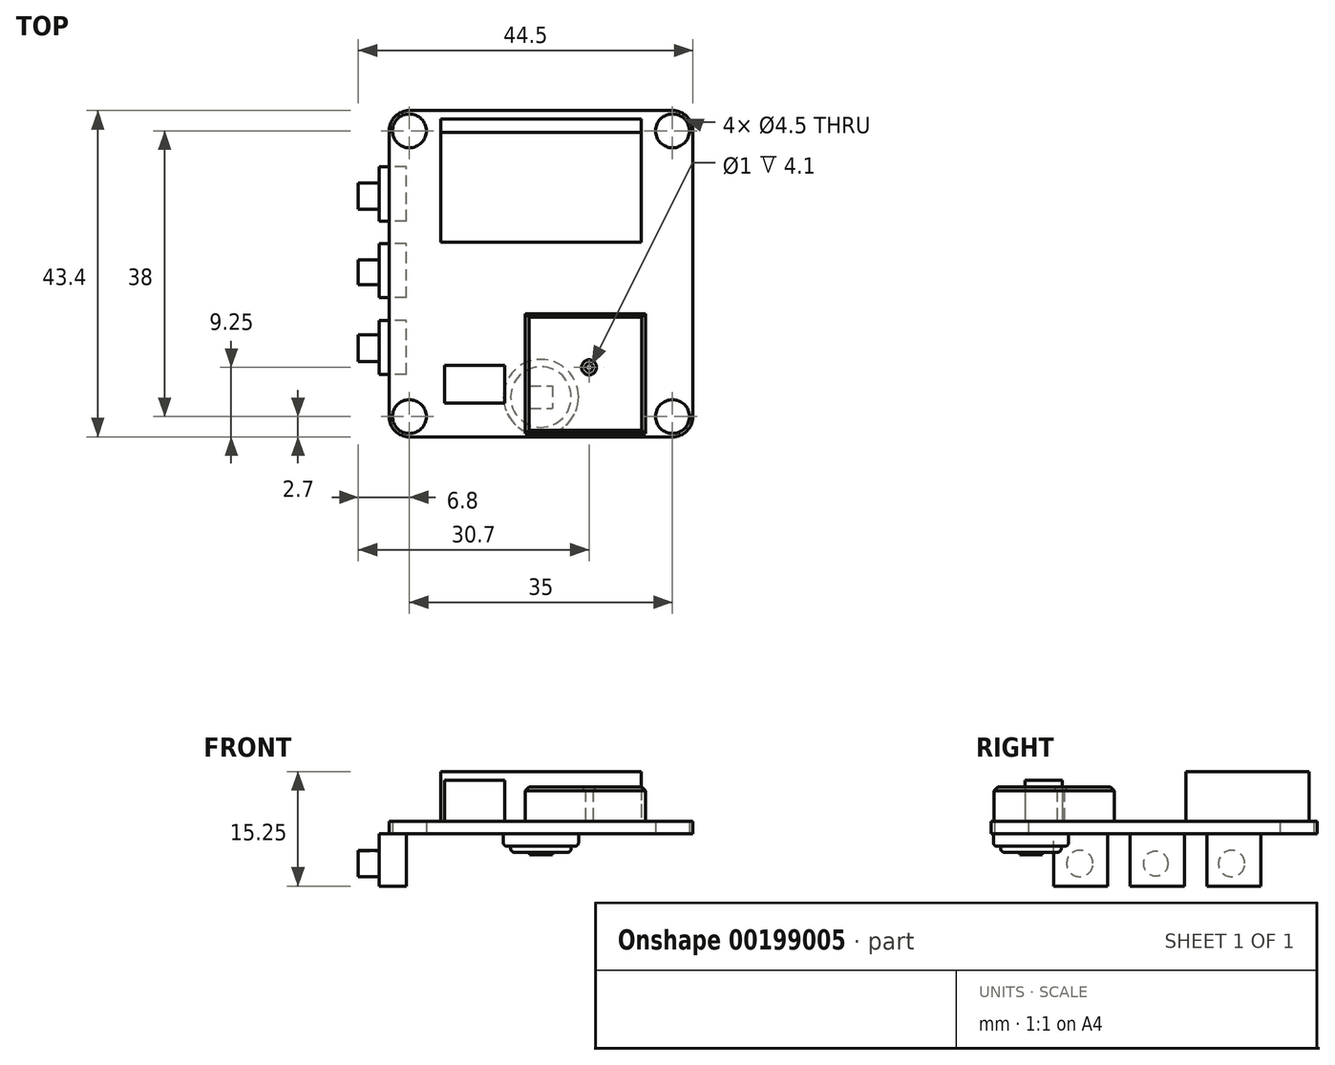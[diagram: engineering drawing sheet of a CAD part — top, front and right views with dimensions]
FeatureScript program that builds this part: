
annotation { "Feature Type Name" : "Feature", "Feature Type Description" : "" }
export const myFeature = defineFeature(function(context is Context, id is Id, definition is map)
    precondition{}
    {
        {
            var Q0;
            Q0=qCreatedBy(makeId("Top.planeOp"),FACE);
            var sketch = newSketch(context, id + "F0", { "sketchPlane" : qUnion([Q0])});
            skLineSegment(sketch, "E0.bottom", {"start": v(17.5, -21.7) * mm, "end": v(-17.5, -21.7) * mm});
            skLineSegment(sketch, "E0.top", {"start": v(17.5, 21.7) * mm, "end": v(-17.5, 21.7) * mm});
            skLineSegment(sketch, "E0.left", {"start": v(20.2, -19) * mm, "end": v(20.2, 19) * mm});
            skLineSegment(sketch, "E0.right", {"start": v(-20.2, -19) * mm, "end": v(-20.2, 19) * mm});
            skPoint(sketch, "E0.middle", {"position": v(0, 0) * mm});
            skPoint(sketch, "E1.visualSharp", {"position": v(-20.2, 21.7) * mm});
            skArc(sketch, "E1.filletArc", {"start": v(-17.5, 21.7) * mm, "mid": v(-19.4, 20.9) * mm, "end": v(-20.2, 19) * mm});
            skPoint(sketch, "E2.visualSharp", {"position": v(-20.2, -21.7) * mm});
            skArc(sketch, "E2.filletArc", {"start": v(-20.2, -19) * mm, "mid": v(-19.4, -20.9) * mm, "end": v(-17.5, -21.7) * mm});
            skPoint(sketch, "E3.visualSharp", {"position": v(20.2, -21.7) * mm});
            skArc(sketch, "E3.filletArc", {"start": v(17.5, -21.7) * mm, "mid": v(19.4, -20.9) * mm, "end": v(20.2, -19) * mm});
            skPoint(sketch, "E4.visualSharp", {"position": v(20.2, 21.7) * mm});
            skArc(sketch, "E4.filletArc", {"start": v(20.2, 19) * mm, "mid": v(19.4, 20.9) * mm, "end": v(17.5, 21.7) * mm});
            skCircle(sketch, "E5", {"center": v(-17.5, 19) * mm, "radius": 2.25 * mm});
            skCircle(sketch, "E6", {"center": v(17.5, 19) * mm, "radius": 2.25 * mm});
            skCircle(sketch, "E7", {"center": v(-17.5, -19) * mm, "radius": 2.25 * mm});
            skCircle(sketch, "E8", {"center": v(-17.5, -19) * mm, "radius": 1.5 * mm});
            skCircle(sketch, "E9", {"center": v(-17.5, 19) * mm, "radius": 1.5 * mm});
            skCircle(sketch, "E10", {"center": v(17.5, -19) * mm, "radius": 2.25 * mm});
            skCircle(sketch, "E11", {"center": v(17.5, -19) * mm, "radius": 1.5 * mm});
            skCircle(sketch, "E12", {"center": v(17.5, 19) * mm, "radius": 1.5 * mm});
            skSolve(sketch);
        }
        {
            var Q0;
            Q0 = qSketchRegion(id + "F0", true);
            extrude(context, id + "F1", {"entities" : qUnion([Q0]), "depth" : 1.6 * mm, "symmetric" : true});
        }
        {
            var Q0;
            Q0=makeQuery(id+"F1.opExtrude","CAP_FACE",FACE,{"disambiguationData":[OSD([sQuery(id+"F0.wireOp",EDGE,"E0.bottom"),sQuery(id+"F0.wireOp",EDGE,"E0.top"),sQuery(id+"F0.wireOp",EDGE,"E0.left"),sQuery(id+"F0.wireOp",EDGE,"E0.right"),sQuery(id+"F0.wireOp",EDGE,"E1.filletArc"),sQuery(id+"F0.wireOp",EDGE,"E2.filletArc"),sQuery(id+"F0.wireOp",EDGE,"E3.filletArc"),sQuery(id+"F0.wireOp",EDGE,"E4.filletArc"),sQuery(id+"F0.wireOp",EDGE,"E5"),sQuery(id+"F0.wireOp",EDGE,"E6"),sQuery(id+"F0.wireOp",EDGE,"E7"),sQuery(id+"F0.wireOp",EDGE,"E10")])],"isStart":false});
            cPlane(context, id + "F2", {"entities" : qUnion([Q0]), "cplaneType" : CPlaneType.OFFSET, "offset" : 0 * mm, "width" : 150 * mm, "height" : 150 * mm});
        }
        {
            var Q0;
            Q0=qCreatedBy(id+"F2.planeOp",FACE);
            var sketch = newSketch(context, id + "F3", { "sketchPlane" : qUnion([Q0])});
            skPoint(sketch, "E13.middle", {"position": v(0, 0) * mm});
            skPoint(sketch, "E14", {"position": v(-8.8, -14.7) * mm});
            skLineSegment(sketch, "E15.bottom", {"start": v(-4.8, -17.2) * mm, "end": v(-12.8, -17.2) * mm});
            skLineSegment(sketch, "E15.top", {"start": v(-4.8, -12.2) * mm, "end": v(-12.8, -12.2) * mm});
            skLineSegment(sketch, "E15.left", {"start": v(-4.8, -17.2) * mm, "end": v(-4.8, -12.2) * mm});
            skLineSegment(sketch, "E15.right", {"start": v(-12.8, -17.2) * mm, "end": v(-12.8, -12.2) * mm});
            skPoint(sketch, "E16", {"position": v(5.9, -13.3) * mm});
            skCircle(sketch, "E17", {"center": v(6.4, -12.45) * mm, "radius": 0.5 * mm});
            skLineSegment(sketch, "E18.bottom", {"start": v(-2.1, -5.3) * mm, "end": v(13.9, -5.3) * mm});
            skLineSegment(sketch, "E18.top", {"start": v(-2.1, -21.3) * mm, "end": v(13.9, -21.3) * mm});
            skLineSegment(sketch, "E18.left", {"start": v(-2.1, -5.3) * mm, "end": v(-2.1, -21.3) * mm});
            skLineSegment(sketch, "E18.right", {"start": v(13.9, -5.3) * mm, "end": v(13.9, -21.3) * mm});
            skLineSegment(sketch, "E19", {"start": v(-20.2, -21.7) * mm, "end": v(-13.35, -21.7) * mm});
            skLineSegment(sketch, "E20", {"start": v(-13.35, -21.7) * mm, "end": v(-13.35, -4.8) * mm});
            skLineSegment(sketch, "E21.bottom", {"start": v(-13.35, -4.8) * mm, "end": v(13.35, -4.8) * mm});
            skLineSegment(sketch, "E21.top", {"start": v(-13.35, 20.6) * mm, "end": v(13.35, 20.6) * mm});
            skLineSegment(sketch, "E21.left", {"start": v(-13.35, -4.8) * mm, "end": v(-13.35, 20.6) * mm});
            skLineSegment(sketch, "E21.right", {"start": v(13.35, -4.8) * mm, "end": v(13.35, 20.6) * mm});
            skLineSegment(sketch, "E22", {"start": v(-13.35, -4.8) * mm, "end": v(-13.35, 4.2) * mm});
            skLineSegment(sketch, "E23.bottom", {"start": v(-13.35, 4.2) * mm, "end": v(13.35, 4.2) * mm});
            skLineSegment(sketch, "E23.top", {"start": v(-13.35, 18.8) * mm, "end": v(13.35, 18.8) * mm});
            skLineSegment(sketch, "E23.left", {"start": v(-13.35, 4.2) * mm, "end": v(-13.35, 18.8) * mm});
            skLineSegment(sketch, "E23.right", {"start": v(13.35, 4.2) * mm, "end": v(13.35, 18.8) * mm});
            skLineSegment(sketch, "E24", {"start": v(-20.2, -21.7) * mm, "end": v(-8.8, -21.7) * mm});
            skLineSegment(sketch, "E25", {"start": v(-8.8, -21.7) * mm, "end": v(-8.8, -14.7) * mm});
            skLineSegment(sketch, "E26", {"start": v(-20.2, -21.7) * mm, "end": v(5.9, -21.7) * mm});
            skLineSegment(sketch, "E27", {"start": v(5.9, -21.7) * mm, "end": v(5.9, -13.3) * mm});
            skLineSegment(sketch, "E28", {"start": v(5.9, -13.3) * mm, "end": v(6.4, -13.3) * mm});
            skLineSegment(sketch, "E29", {"start": v(6.4, -13.3) * mm, "end": v(6.4, -12.45) * mm});
            skLineSegment(sketch, "E30", {"start": v(-20.2, -21.7) * mm, "end": v(-17.9, -21.7) * mm});
            skLineSegment(sketch, "E31", {"start": v(0, 0) * mm, "end": v(0, -21.7) * mm});
            skSolve(sketch);
        }
        {
            var Q0;
            {var subQ0=sQuery(id+"F3.wireOp",EDGE,"E18.left");Q0=makeQuery(id+"F3.imprint","IMPRINT",FACE,{"disambiguationData":[TD([[makeQuery(id+"F3.imprint","IMPRINT",EDGE,{"derivedFrom":subQ0}),1.0]])]});}
            var Q1;
            Q1=makeQuery(id+"F3.imprint","IMPRINT",FACE,{"disambiguationData":[TD([[makeQuery(id+"F3.imprint","IMPRINT",EDGE,{"derivedFrom":sQuery(id+"F3.wireOp",EDGE,"E17")}),-1.0]])]});
            extrude(context, id + "F4", {"entities" : qUnion([Q0, Q1]), "operationType" : NewBodyOperationType.ADD, "depth" : 4.6 * mm});
        }
        {
            var Q0;
            Q0=makeQuery(id+"F3.imprint","IMPRINT",FACE,{"disambiguationData":[TD([[makeQuery(id+"F3.imprint","IMPRINT",EDGE,{"derivedFrom":sQuery(id+"F3.wireOp",EDGE,"E15.top")}),1.0]])]});
            extrude(context, id + "F5", {"entities" : qUnion([Q0]), "operationType" : NewBodyOperationType.ADD, "depth" : 5.5 * mm});
        }
        {
            var Q0;
            {var subQ0=sQuery(id+"F3.wireOp",EDGE,"E21.top");Q0=makeQuery(id+"F3.imprint","IMPRINT",FACE,{"disambiguationData":[TD([[makeQuery(id+"F3.imprint","IMPRINT",EDGE,{"derivedFrom":subQ0}),-1.0]])]});}
            var Q1;
            {var subQ4=sQuery(id+"F3.wireOp",EDGE,"E22");Q1=makeQuery(id+"F3.imprint","IMPRINT",FACE,{"disambiguationData":[TD([[makeQuery(id+"F3.imprint","IMPRINT",EDGE,{"derivedFrom":subQ4}),-1.0]])]});}
            extrude(context, id + "F6", {"entities" : qUnion([Q0, Q1]), "operationType" : NewBodyOperationType.ADD, "depth" : 6.6 * mm});
        }
        {
            var Q0;
            Q0=makeQuery(id+"F3.imprint","IMPRINT",FACE,{"disambiguationData":[TD([[makeQuery(id+"F3.imprint","IMPRINT",EDGE,{"derivedFrom":sQuery(id+"F3.wireOp",EDGE,"E23.bottom")}),1.0]])]});
            extrude(context, id + "F7", {"entities" : qUnion([Q0]), "operationType" : NewBodyOperationType.ADD, "depth" : 6.65 * mm});
        }
        {
            var Q0;
            Q0=makeQuery(id+"F1.opExtrude","CAP_FACE",FACE,{"disambiguationData":[OSD([sQuery(id+"F0.wireOp",EDGE,"E0.bottom"),sQuery(id+"F0.wireOp",EDGE,"E0.top"),sQuery(id+"F0.wireOp",EDGE,"E0.left"),sQuery(id+"F0.wireOp",EDGE,"E0.right"),sQuery(id+"F0.wireOp",EDGE,"E1.filletArc"),sQuery(id+"F0.wireOp",EDGE,"E2.filletArc"),sQuery(id+"F0.wireOp",EDGE,"E3.filletArc"),sQuery(id+"F0.wireOp",EDGE,"E4.filletArc"),sQuery(id+"F0.wireOp",EDGE,"E5"),sQuery(id+"F0.wireOp",EDGE,"E6"),sQuery(id+"F0.wireOp",EDGE,"E7"),sQuery(id+"F0.wireOp",EDGE,"E10")])],"isStart":true});
            cPlane(context, id + "F8", {"entities" : qUnion([Q0]), "cplaneType" : CPlaneType.OFFSET, "offset" : 0 * mm, "width" : 150 * mm, "height" : 150 * mm});
        }
        {
            var Q0;
            Q0=qCreatedBy(id+"F8.planeOp",FACE);
            var sketch = newSketch(context, id + "F9", { "sketchPlane" : qUnion([Q0])});
            skPoint(sketch, "E32.middle", {"position": v(0, 0) * mm});
            skLineSegment(sketch, "E33", {"start": v(0, 0) * mm, "end": v(0, 21.7) * mm});
            skLineSegment(sketch, "E34", {"start": v(0, 21.7) * mm, "end": v(-20.2, 21.7) * mm});
            skLineSegment(sketch, "E35", {"start": v(-20.2, 21.7) * mm, "end": v(-17.9, 21.7) * mm});
            skLineSegment(sketch, "E36", {"start": v(-17.9, 21.7) * mm, "end": v(-17.9, 13.4) * mm});
            skLineSegment(sketch, "E37.bottom", {"start": v(-17.9, 13.4) * mm, "end": v(-21.5, 13.4) * mm});
            skLineSegment(sketch, "E37.top", {"start": v(-17.9, 6.2) * mm, "end": v(-21.5, 6.2) * mm});
            skLineSegment(sketch, "E37.left", {"start": v(-17.9, 13.4) * mm, "end": v(-17.9, 6.2) * mm});
            skLineSegment(sketch, "E37.right", {"start": v(-21.5, 13.4) * mm, "end": v(-21.5, 6.2) * mm});
            skLineSegment(sketch, "E38", {"start": v(-17.9, 6.2) * mm, "end": v(-17.9, 3.2) * mm});
            skLineSegment(sketch, "E39.bottom", {"start": v(-17.9, 3.2) * mm, "end": v(-21.5, 3.2) * mm});
            skLineSegment(sketch, "E39.top", {"start": v(-17.9, -4) * mm, "end": v(-21.5, -4) * mm});
            skLineSegment(sketch, "E39.left", {"start": v(-17.9, 3.2) * mm, "end": v(-17.9, -4) * mm});
            skLineSegment(sketch, "E39.right", {"start": v(-21.5, 3.2) * mm, "end": v(-21.5, -4) * mm});
            skLineSegment(sketch, "E40", {"start": v(-17.9, -4) * mm, "end": v(-17.9, -7) * mm});
            skLineSegment(sketch, "E41.bottom", {"start": v(-17.9, -7) * mm, "end": v(-21.5, -7) * mm});
            skLineSegment(sketch, "E41.top", {"start": v(-17.9, -14.2) * mm, "end": v(-21.5, -14.2) * mm});
            skLineSegment(sketch, "E41.left", {"start": v(-17.9, -7) * mm, "end": v(-17.9, -14.2) * mm});
            skLineSegment(sketch, "E41.right", {"start": v(-21.5, -7) * mm, "end": v(-21.5, -14.2) * mm});
            skLineSegment(sketch, "E42", {"start": v(0, 21.7) * mm, "end": v(0, 16.4) * mm});
            skCircle(sketch, "E43", {"center": v(0, 16.4) * mm, "radius": 5 * mm});
            skCircle(sketch, "E44", {"center": v(0, 16.4) * mm, "radius": 4.03 * mm});
            skLineSegment(sketch, "E45.bottom", {"start": v(-1.5, 14.9) * mm, "end": v(1.5, 14.9) * mm});
            skLineSegment(sketch, "E45.top", {"start": v(-1.5, 17.9) * mm, "end": v(1.5, 17.9) * mm});
            skLineSegment(sketch, "E45.left", {"start": v(-1.5, 14.9) * mm, "end": v(-1.5, 17.9) * mm});
            skLineSegment(sketch, "E45.right", {"start": v(1.5, 14.9) * mm, "end": v(1.5, 17.9) * mm});
            skSolve(sketch);
        }
        {
            var Q0;
            Q0=makeQuery(id+"F9.imprint","IMPRINT",FACE,{"disambiguationData":[TD([[makeQuery(id+"F9.imprint","IMPRINT",EDGE,{"derivedFrom":sQuery(id+"F9.wireOp",EDGE,"E41.bottom")}),1.0]])]});
            var Q1;
            Q1=makeQuery(id+"F9.imprint","IMPRINT",FACE,{"disambiguationData":[TD([[makeQuery(id+"F9.imprint","IMPRINT",EDGE,{"derivedFrom":sQuery(id+"F9.wireOp",EDGE,"E39.bottom")}),1.0]])]});
            var Q2;
            Q2=makeQuery(id+"F9.imprint","IMPRINT",FACE,{"disambiguationData":[TD([[makeQuery(id+"F9.imprint","IMPRINT",EDGE,{"derivedFrom":sQuery(id+"F9.wireOp",EDGE,"E37.bottom")}),1.0]])]});
            extrude(context, id + "F10", {"entities" : qUnion([Q0, Q1, Q2]), "operationType" : NewBodyOperationType.ADD, "depth" : 7 * mm});
        }
        {
            var Q0;
            Q0=makeQuery(id+"F1.opExtrude","CAP_FACE",FACE,{"disambiguationData":[OSD([sQuery(id+"F0.wireOp",EDGE,"E0.bottom"),sQuery(id+"F0.wireOp",EDGE,"E0.top"),sQuery(id+"F0.wireOp",EDGE,"E0.left"),sQuery(id+"F0.wireOp",EDGE,"E0.right"),sQuery(id+"F0.wireOp",EDGE,"E1.filletArc"),sQuery(id+"F0.wireOp",EDGE,"E2.filletArc"),sQuery(id+"F0.wireOp",EDGE,"E3.filletArc"),sQuery(id+"F0.wireOp",EDGE,"E4.filletArc"),sQuery(id+"F0.wireOp",EDGE,"E5"),sQuery(id+"F0.wireOp",EDGE,"E6"),sQuery(id+"F0.wireOp",EDGE,"E7"),sQuery(id+"F0.wireOp",EDGE,"E10")])],"isStart":true});
            cPlane(context, id + "F11", {"entities" : qUnion([Q0]), "cplaneType" : CPlaneType.OFFSET, "offset" : 4 * mm, "width" : 150 * mm, "height" : 150 * mm});
        }
        {
            var Q0;
            Q0=qCreatedBy(id+"F11.planeOp",FACE);
            var sketch = newSketch(context, id + "F12", { "sketchPlane" : qUnion([Q0])});
            skLineSegment(sketch, "E46", {"start": v(0, 0) * mm, "end": v(0, 21.7) * mm});
            skLineSegment(sketch, "E47", {"start": v(0, 21.7) * mm, "end": v(-20.2, 21.7) * mm});
            skLineSegment(sketch, "E48", {"start": v(-20.2, 21.7) * mm, "end": v(-21, 21.7) * mm});
            skLineSegment(sketch, "E49", {"start": v(-21, 21.7) * mm, "end": v(-21, 11.65) * mm});
            skLineSegment(sketch, "E50.bottom", {"start": v(-21, 11.65) * mm, "end": v(-24.3, 11.65) * mm});
            skLineSegment(sketch, "E50.top", {"start": v(-21, 8.15) * mm, "end": v(-24.3, 8.15) * mm});
            skLineSegment(sketch, "E50.left", {"start": v(-21, 11.65) * mm, "end": v(-21, 8.15) * mm});
            skLineSegment(sketch, "E50.right", {"start": v(-24.3, 11.65) * mm, "end": v(-24.3, 8.15) * mm});
            skLineSegment(sketch, "E51", {"start": v(-21, 8.15) * mm, "end": v(-21, 1.45) * mm});
            skLineSegment(sketch, "E52.bottom", {"start": v(-21, 1.45) * mm, "end": v(-24.3, 1.45) * mm});
            skLineSegment(sketch, "E52.top", {"start": v(-21, -1.85) * mm, "end": v(-24.3, -1.85) * mm});
            skLineSegment(sketch, "E52.left", {"start": v(-21, 1.45) * mm, "end": v(-21, -1.85) * mm});
            skLineSegment(sketch, "E52.right", {"start": v(-24.3, 1.45) * mm, "end": v(-24.3, -1.85) * mm});
            skLineSegment(sketch, "E53", {"start": v(-21, -1.85) * mm, "end": v(-21, -8.55) * mm});
            skLineSegment(sketch, "E54.bottom", {"start": v(-21, -8.55) * mm, "end": v(-24.3, -8.55) * mm});
            skLineSegment(sketch, "E54.top", {"start": v(-21, -12.05) * mm, "end": v(-24.3, -12.05) * mm});
            skLineSegment(sketch, "E54.left", {"start": v(-21, -8.55) * mm, "end": v(-21, -12.05) * mm});
            skLineSegment(sketch, "E54.right", {"start": v(-24.3, -8.55) * mm, "end": v(-24.3, -12.05) * mm});
            skLineSegment(sketch, "E55", {"start": v(-21, -10.3) * mm, "end": v(-24.3, -10.3) * mm});
            skLineSegment(sketch, "E56", {"start": v(-21, -0.2) * mm, "end": v(-24.3, -0.2) * mm});
            skLineSegment(sketch, "E57", {"start": v(-21, 9.9) * mm, "end": v(-24.3, 9.9) * mm});
            skSolve(sketch);
        }
        {
            var Q0;
            {var subQ0=sQuery(id+"F12.wireOp",EDGE,"E50.top");Q0=makeQuery(id+"F12.imprint","IMPRINT",FACE,{"disambiguationData":[TD([[makeQuery(id+"F12.imprint","IMPRINT",EDGE,{"derivedFrom":subQ0}),-1.0]])]});}
            var Q1;
            Q1=sQuery(id+"F12.wireOp",EDGE,"E57");
            revolve(context, id + "F13", {"operationType" : NewBodyOperationType.ADD, "entities" : qUnion([Q0]), "axis" : qUnion([Q1]), "revolveType" : RevolveType.FULL});
        }
        {
            var Q0;
            {var subQ0=sQuery(id+"F12.wireOp",EDGE,"E52.top");Q0=makeQuery(id+"F12.imprint","IMPRINT",FACE,{"disambiguationData":[TD([[makeQuery(id+"F12.imprint","IMPRINT",EDGE,{"derivedFrom":subQ0}),-1.0]])]});}
            var Q1;
            Q1=sQuery(id+"F12.wireOp",EDGE,"E56");
            revolve(context, id + "F14", {"operationType" : NewBodyOperationType.ADD, "entities" : qUnion([Q0]), "axis" : qUnion([Q1]), "revolveType" : RevolveType.FULL});
        }
        {
            var Q0;
            {var subQ0=sQuery(id+"F12.wireOp",EDGE,"E54.top");Q0=makeQuery(id+"F12.imprint","IMPRINT",FACE,{"disambiguationData":[TD([[makeQuery(id+"F12.imprint","IMPRINT",EDGE,{"derivedFrom":subQ0}),-1.0]])]});}
            var Q1;
            Q1=sQuery(id+"F12.wireOp",EDGE,"E55");
            revolve(context, id + "F15", {"operationType" : NewBodyOperationType.ADD, "entities" : qUnion([Q0]), "axis" : qUnion([Q1]), "revolveType" : RevolveType.FULL});
        }
        {
            var Q0;
            {var subQ5=sQuery(id+"F9.wireOp",EDGE,"E45.right");Q0=makeQuery(id+"F9.imprint","IMPRINT",FACE,{"disambiguationData":[TD([[makeQuery(id+"F9.imprint","IMPRINT",EDGE,{"derivedFrom":subQ5}),-1.0]])]});}
            var Q1;
            {var subQ0=sQuery(id+"F9.wireOp",EDGE,"E45.left");Q1=makeQuery(id+"F9.imprint","IMPRINT",FACE,{"disambiguationData":[TD([[makeQuery(id+"F9.imprint","IMPRINT",EDGE,{"derivedFrom":subQ0}),1.0]])]});}
            extrude(context, id + "F16", {"entities" : qUnion([Q0, Q1]), "operationType" : NewBodyOperationType.ADD, "depth" : 2.5 * mm});
        }
        {
            var Q0;
            {var subQ0=sQuery(id+"F9.wireOp",EDGE,"E43");var subQ1=sQuery(id+"F9.wireOp",EDGE,"E33");var subQ2=makeQuery(id+"F9.imprint","INTERSECT",VERTEX,{"derivedFrom":[subQ1,subQ0]});Q0=makeQuery(id+"F9.imprint","IMPRINT",FACE,{"disambiguationData":[TD([[makeQuery(id+"F9.imprint","IMPRINT",EDGE,{"disambiguationData":[TD([[subQ2,-1.0]])],"derivedFrom":subQ1}),-1.0]])]});}
            var Q1;
            {var subQ0=sQuery(id+"F9.wireOp",EDGE,"E43");var subQ1=sQuery(id+"F9.wireOp",EDGE,"E33");var subQ2=makeQuery(id+"F9.imprint","INTERSECT",VERTEX,{"derivedFrom":[subQ1,subQ0]});Q1=makeQuery(id+"F9.imprint","IMPRINT",FACE,{"disambiguationData":[TD([[makeQuery(id+"F9.imprint","IMPRINT",EDGE,{"disambiguationData":[TD([[subQ2,-1.0]])],"derivedFrom":subQ1}),1.0]])]});}
            extrude(context, id + "F17", {"entities" : qUnion([Q0, Q1]), "operationType" : NewBodyOperationType.ADD, "depth" : 1.7 * mm});
        }
        {
            var Q0;
            Q0=makeQuery(id+"F17.opExtrude","CAP_EDGE",EDGE,{"disambiguationData":[OSD([sQuery(id+"F9.wireOp",EDGE,"E43")])],"isStart":false});
            var Q1;
            Q1=makeQuery(id+"F16.opExtrude","CAP_EDGE",EDGE,{"disambiguationData":[OSD([sQuery(id+"F9.wireOp",EDGE,"E44")])],"isStart":false});
            fillet(context, id + "F18", {"entities" : qUnion([Q0, Q1]), "radius" : 0.5 * mm, "tangentPropagation" : true, "allowEdgeOverflow" : false});
        }
        {
            var Q0;
            Q0=makeQuery(id+"F4.opExtrude","CAP_FACE",FACE,{"disambiguationData":[OSD([sQuery(id+"F3.wireOp",EDGE,"E17"),sQuery(id+"F3.wireOp",EDGE,"E18.bottom"),sQuery(id+"F3.wireOp",EDGE,"E18.top"),sQuery(id+"F3.wireOp",EDGE,"E18.left"),sQuery(id+"F3.wireOp",EDGE,"E18.right")])],"isStart":false});
            chamfer(context, id + "F19", {"entities" : qUnion([Q0]), "width" : 0.5 * mm, "tangentPropagation" : true});
        }
        {
            var Q0;
            {var subQ0=sQuery(id+"F9.wireOp",EDGE,"E45.right");Q0=makeQuery(id+"F9.imprint","IMPRINT",FACE,{"disambiguationData":[TD([[makeQuery(id+"F9.imprint","IMPRINT",EDGE,{"derivedFrom":subQ0}),1.0]])]});}
            var Q1;
            {var subQ0=sQuery(id+"F9.wireOp",EDGE,"E45.left");Q1=makeQuery(id+"F9.imprint","IMPRINT",FACE,{"disambiguationData":[TD([[makeQuery(id+"F9.imprint","IMPRINT",EDGE,{"derivedFrom":subQ0}),-1.0]])]});}
            extrude(context, id + "F20", {"entities" : qUnion([Q0, Q1]), "operationType" : NewBodyOperationType.ADD, "depth" : 2.8 * mm});
        }
    });
